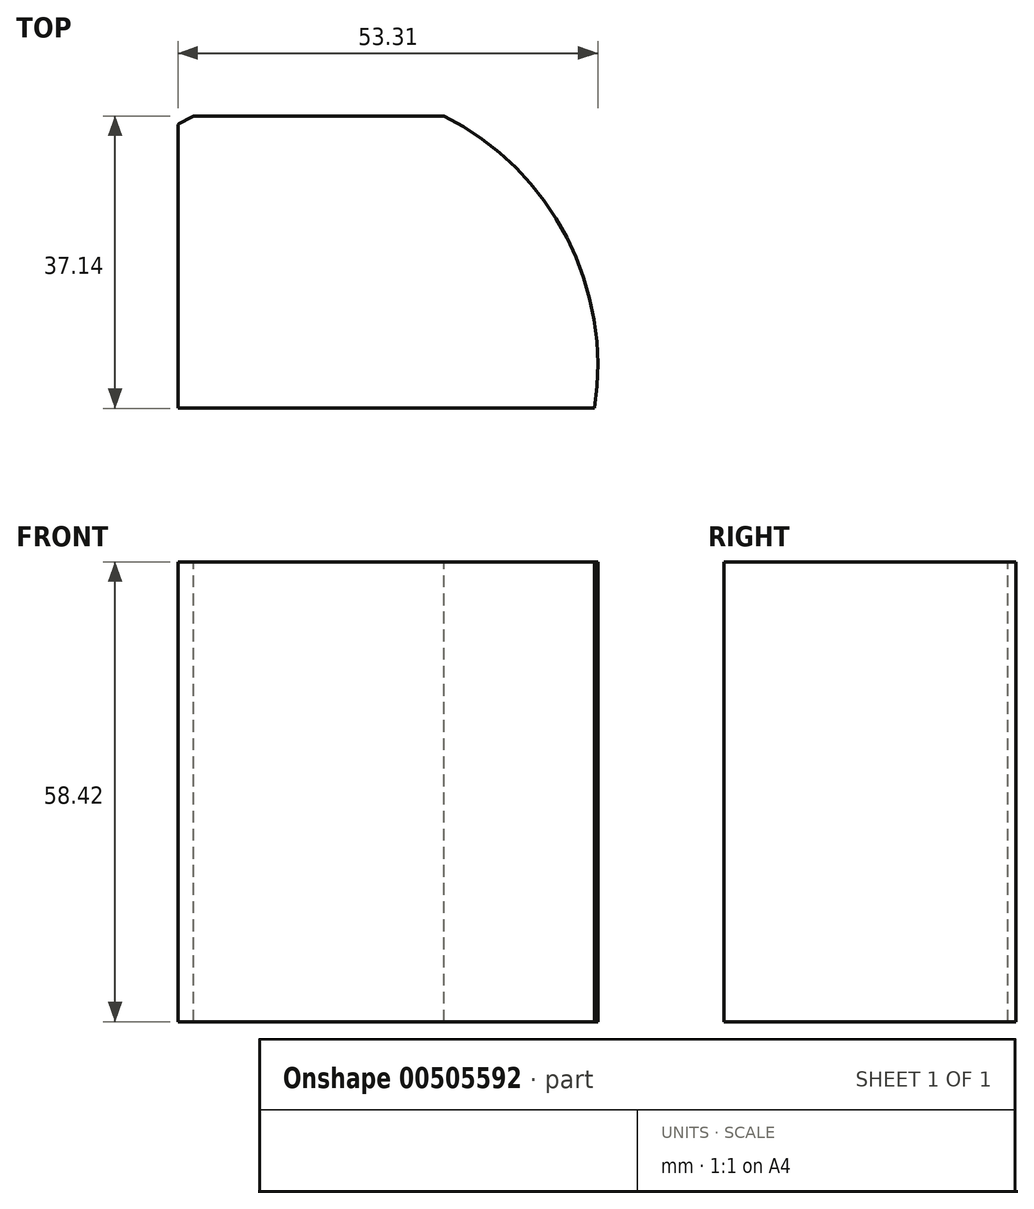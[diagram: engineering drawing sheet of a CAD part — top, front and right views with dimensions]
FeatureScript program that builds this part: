
annotation { "Feature Type Name" : "Feature", "Feature Type Description" : "" }
export const myFeature = defineFeature(function(context is Context, id is Id, definition is map)
    precondition{}
    {
        {
            var Q0;
            Q0=qCreatedBy(makeId("Top.planeOp"),FACE);
            var sketch = newSketch(context, id + "F0", { "sketchPlane" : qUnion([Q0])});
            skLineSegment(sketch, "E0.bottom", {"start": v(33.98, -5.47) * mm, "end": v(-20.15, -5.47) * mm});
            skLineSegment(sketch, "E0.top", {"start": v(33.98, 31.67) * mm, "end": v(-20.15, 31.67) * mm});
            skLineSegment(sketch, "E0.left", {"start": v(33.98, -5.47) * mm, "end": v(33.98, 31.67) * mm});
            skLineSegment(sketch, "E0.right", {"start": v(-20.15, -5.47) * mm, "end": v(-20.15, 31.67) * mm});
            skCircle(sketch, "E1", {"center": v(-2.28, 0) * mm, "radius": 35.44 * mm});
            skSolve(sketch);
        }
        {
            var Q0;
            {var subQ3=sQuery(id+"F0.wireOp",EDGE,"E0.right");var subQ6=sQuery(id+"F0.wireOp",EDGE,"E0.bottom");var subQ7=makeQuery(id+"F0.imprint","INTERSECT",VERTEX,{"derivedFrom":[subQ6,subQ3]});Q0=makeQuery(id+"F0.imprint","IMPRINT",FACE,{"disambiguationData":[TD([[makeQuery(id+"F0.imprint","IMPRINT",EDGE,{"disambiguationData":[TD([[subQ7,1.0]])],"derivedFrom":subQ6}),-1.0]])]});}
            extrude(context, id + "F1", {"entities" : qUnion([Q0]), "oppositeDirection" : true, "depth" : 58.42 * mm});
        }
    });
